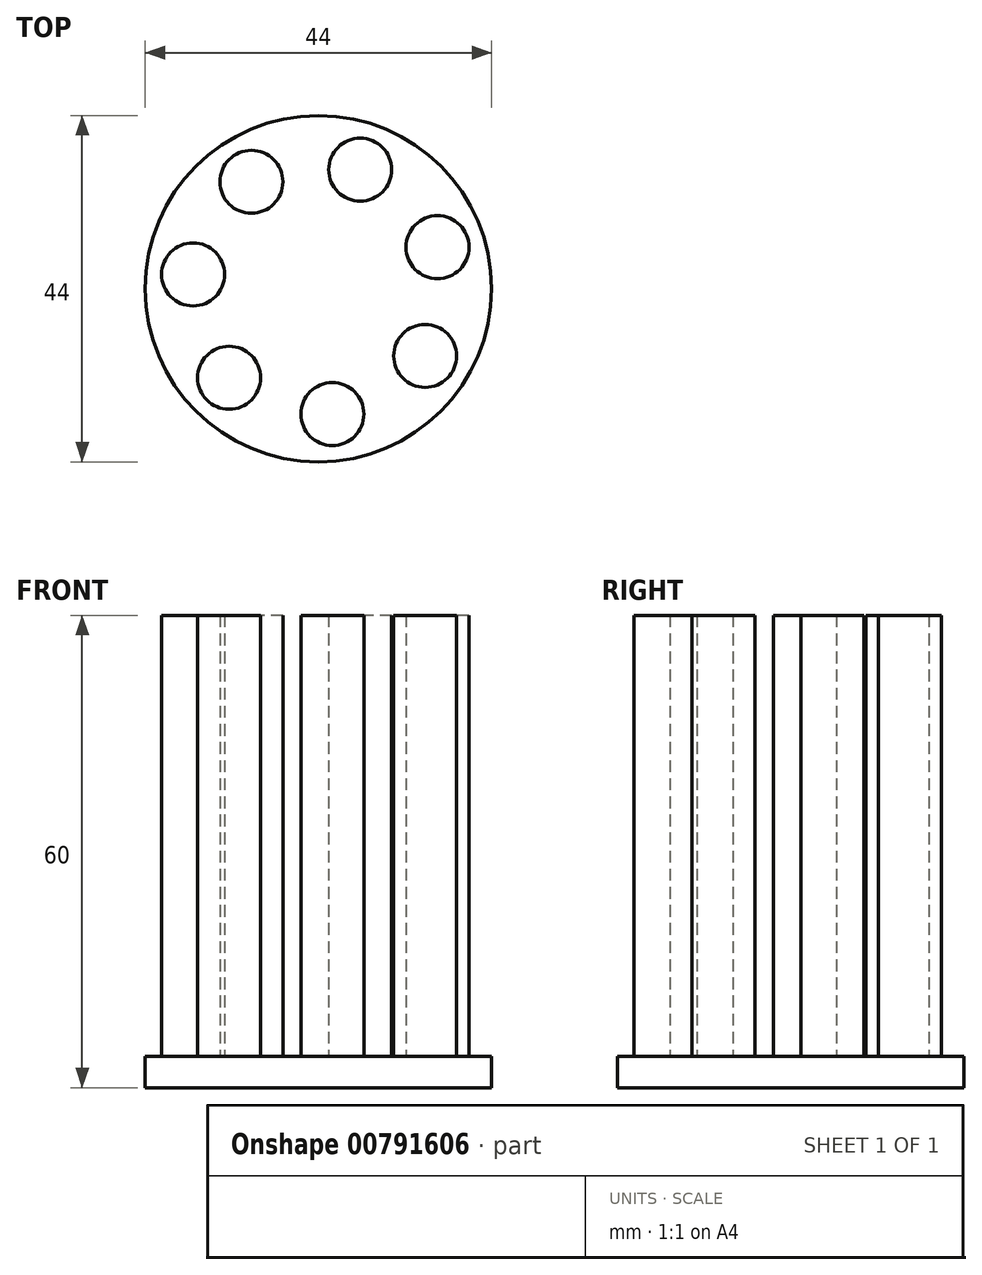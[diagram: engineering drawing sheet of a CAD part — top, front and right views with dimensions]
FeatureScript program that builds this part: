
annotation { "Feature Type Name" : "Feature", "Feature Type Description" : "" }
export const myFeature = defineFeature(function(context is Context, id is Id, definition is map)
    precondition{}
    {
        {
            var Q0;
            Q0=qCreatedBy(makeId("Top.planeOp"),FACE);
            var sketch = newSketch(context, id + "F0", { "sketchPlane" : qUnion([Q0])});
            skCircle(sketch, "E0", {"center": v(0, 0) * mm, "radius": 22 * mm});
            skLineSegment(sketch, "E1", {"start": v(0, 0) * mm, "end": v(13.56, -8.54) * mm, "construction": true});
            skCircle(sketch, "E2", {"center": v(13.56, -8.54) * mm, "radius": 4 * mm});
            skCircle(sketch, "E3.1.0", {"center": v(15.13, 5.27) * mm, "radius": 4 * mm});
            skCircle(sketch, "E3.2.0", {"center": v(5.31, 15.12) * mm, "radius": 4 * mm});
            skCircle(sketch, "E3.3.0", {"center": v(-8.5, 13.58) * mm, "radius": 4 * mm});
            skCircle(sketch, "E3.4.0", {"center": v(-15.92, 1.81) * mm, "radius": 4 * mm});
            skCircle(sketch, "E3.5.0", {"center": v(-11.34, -11.32) * mm, "radius": 4 * mm});
            skCircle(sketch, "E3.6.0", {"center": v(1.78, -15.93) * mm, "radius": 4 * mm});
            skSolve(sketch);
        }
        {
            var Q0;
            Q0 = qSketchRegion(id + "F0", true);
            extrude(context, id + "F1", {"entities" : qUnion([Q0]), "depth" : 4 * mm, "offsetDistance" : 25.4 * mm});
        }
        {
            var Q0;
            Q0=makeQuery(id+"F0.imprint","IMPRINT",FACE,{"disambiguationData":[TD([[makeQuery(id+"F0.imprint","IMPRINT",EDGE,{"derivedFrom":sQuery(id+"F0.wireOp",EDGE,"E2")}),1.0]])]});
            var Q1;
            Q1=makeQuery(id+"F0.imprint","IMPRINT",FACE,{"disambiguationData":[TD([[makeQuery(id+"F0.imprint","IMPRINT",EDGE,{"derivedFrom":sQuery(id+"F0.wireOp",EDGE,"E3.3.0")}),1.0]])]});
            var Q2;
            Q2=makeQuery(id+"F0.imprint","IMPRINT",FACE,{"disambiguationData":[TD([[makeQuery(id+"F0.imprint","IMPRINT",EDGE,{"derivedFrom":sQuery(id+"F0.wireOp",EDGE,"E3.1.0")}),1.0]])]});
            var Q3;
            Q3=makeQuery(id+"F0.imprint","IMPRINT",FACE,{"disambiguationData":[TD([[makeQuery(id+"F0.imprint","IMPRINT",EDGE,{"derivedFrom":sQuery(id+"F0.wireOp",EDGE,"E3.5.0")}),1.0]])]});
            var Q4;
            Q4=makeQuery(id+"F0.imprint","IMPRINT",FACE,{"disambiguationData":[TD([[makeQuery(id+"F0.imprint","IMPRINT",EDGE,{"derivedFrom":sQuery(id+"F0.wireOp",EDGE,"E3.6.0")}),1.0]])]});
            var Q5;
            Q5=makeQuery(id+"F0.imprint","IMPRINT",FACE,{"disambiguationData":[TD([[makeQuery(id+"F0.imprint","IMPRINT",EDGE,{"derivedFrom":sQuery(id+"F0.wireOp",EDGE,"E3.4.0")}),1.0]])]});
            var Q6;
            Q6=makeQuery(id+"F0.imprint","IMPRINT",FACE,{"disambiguationData":[TD([[makeQuery(id+"F0.imprint","IMPRINT",EDGE,{"derivedFrom":sQuery(id+"F0.wireOp",EDGE,"E3.2.0")}),1.0]])]});
            extrude(context, id + "F2", {"entities" : qUnion([Q0, Q1, Q2, Q3, Q4, Q5, Q6]), "operationType" : NewBodyOperationType.ADD, "depth" : 60 * mm, "offsetDistance" : 25.4 * mm});
        }
    });
